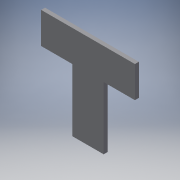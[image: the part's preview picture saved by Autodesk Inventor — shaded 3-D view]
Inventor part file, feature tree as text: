
AUTODESK INVENTOR PART (.ipt)
format: ipt  version: 2017 (Build 210142000, 142)  size: 142,848 bytes
history: native  units: in
note: dims shown in document units (in); Inventor stores cm internally (conversion verified against a paired STEP export)
features: fillet x4, extrude x2, sketch x2
ambient origin geometry x8: Origin, YZ Plane, XZ Plane, XY Plane, X Axis, Y Axis, Z Axis, Center Point
bodies: Solid1 (feature_tree)
feature tree (8):
  extrude  "Extrusion1"  Depth=1.0in
  fillet  "Fillet1"  Radius=1.0in
  fillet  "Fillet2"  Radius=1.0in
  fillet  "Fillet3"  Radius=2.0in
  fillet  "Fillet4"  Radius=1.0in
  extrude  "Extrusion2"  Depth=0.125in
  sketch  "Sketch1"  dims[d0=3.0in d1=1.0in d2=1.0in d3=1.0in d4=2.0in d5=1.0in]
  sketch  "Sketch2"  dims[d6=0.125in d7=0.0in d8=0.125in d9=0.125in d10=0.125in d11=0.125in d12=0.25in d13=0.5in d14=1.1811in d16=1.0in d17=0.3937in d19=1.0in d21=1.1811in d23=1.0in d24=0.3937in d26=1.0in d28=0.125in d29=0.0in]
